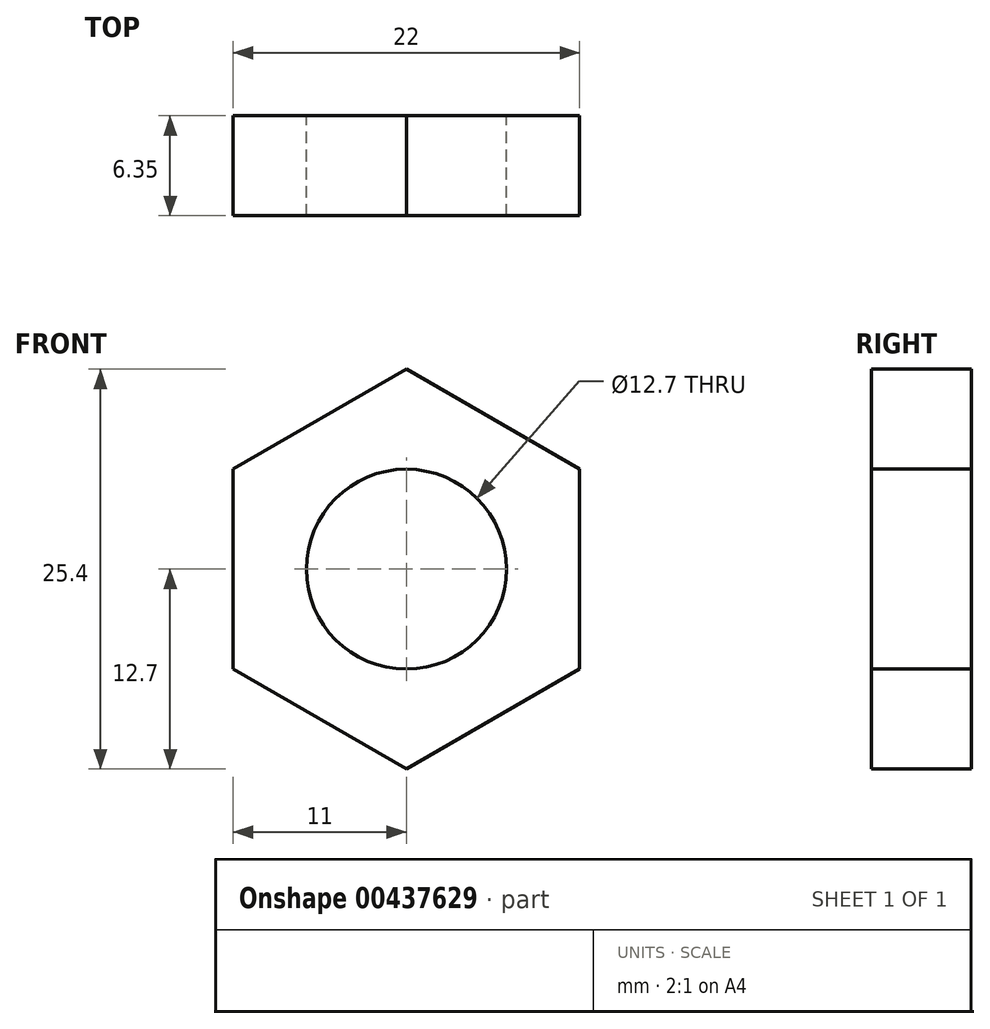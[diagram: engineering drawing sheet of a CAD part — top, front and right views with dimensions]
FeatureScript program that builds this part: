
annotation { "Feature Type Name" : "Feature", "Feature Type Description" : "" }
export const myFeature = defineFeature(function(context is Context, id is Id, definition is map)
    precondition{}
    {
        {
            var Q0;
            Q0=qCreatedBy(makeId("Front.planeOp"),FACE);
            var sketch = newSketch(context, id + "F0", { "sketchPlane" : qUnion([Q0])});
            skCircle(sketch, "E0", {"center": v(0, 0) * mm, "radius": 6.35 * mm});
            skCircle(sketch, "E1.cCircle", {"center": v(0, 0) * mm, "radius": 11 * mm, "construction": true});
            skLineSegment(sketch, "E1.0", {"start": v(11, 6.35) * mm, "end": v(11, -6.35) * mm});
            skLineSegment(sketch, "E1.1", {"start": v(11, -6.35) * mm, "end": v(0, -12.7) * mm});
            skLineSegment(sketch, "E1.2", {"start": v(0, -12.7) * mm, "end": v(-11, -6.35) * mm});
            skLineSegment(sketch, "E1.3", {"start": v(-11, -6.35) * mm, "end": v(-11, 6.35) * mm});
            skLineSegment(sketch, "E1.4", {"start": v(-11, 6.35) * mm, "end": v(0, 12.7) * mm});
            skLineSegment(sketch, "E1.5", {"start": v(0, 12.7) * mm, "end": v(11, 6.35) * mm});
            skPoint(sketch, "E1.0.midPoint", {"position": v(11, 0) * mm});
            skSolve(sketch);
        }
        {
            var Q0;
            Q0 = qSketchRegion(id + "F0", true);
            extrude(context, id + "F1", {"entities" : qUnion([Q0]), "depth" : 6.35 * mm});
        }
    });
